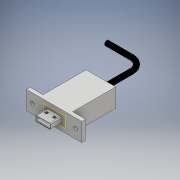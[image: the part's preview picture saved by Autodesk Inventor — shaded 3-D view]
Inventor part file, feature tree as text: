
AUTODESK INVENTOR PART (.ipt)
format: ipt  version: 2018 (Build 220112000, 112)  size: 487,424 bytes
history: native  units: mm
features: sketch x15, extrude x12, fillet x4, plane x2, projected_geometry x2, chamfer x1, sweep x1
ambient origin geometry x8: Origin, YZ Plane, XZ Plane, XY Plane, X Axis, Y Axis, Z Axis, Center Point
bodies: Solid1 (feature_tree)
feature tree (37):
  extrude  "Extrusion1"  Depth=20.88mm
  chamfer  "Chamfer1"  Distance=8.0mm
  fillet  "Fillet1"  Radius=0.5mm
  fillet  "Fillet2"  Radius=3.0mm
  fillet  "Fillet3"  Radius=3.0mm
  extrude  "Extrusion2"  Depth=14.9mm
  extrude  "Extrusion3"  Depth=12.0mm TaperAngle=0.0deg
  fillet  "Fillet4"  Radius=12.0mm
  extrude  "Extrusion4"  Depth=12.0mm TaperAngle=0.0deg
  extrude  "Extrusion5"  Depth=5.0mm
  extrude  "Extrusion6"  Depth=2.0mm
  extrude  "Extrusion7"  Depth=1.8mm
  extrude  "Extrusion8"  Depth=2.45mm TaperAngle=0.0deg
  extrude  "Extrusion9"  Depth=0.2mm TaperAngle=0.0deg
  sketch  "Sketch11"  dims[d27=2.0mm d28=1.8mm]
  plane  "Work Plane1"
  sweep  "Sweep1"
  plane  "Work Plane2"
  sketch  "Sketch13"  dims[d32=0.3mm d33=0.2mm d34=0.0mm]
  extrude  "Extrusion10"  Depth=9.0mm TaperAngle=0.0deg
  extrude  "Extrusion11"  Depth=3.0mm
  extrude  "Extrusion12"  Depth=3.0mm
  sketch  "Sketch1"  dims[d2=16.16mm d3=20.88mm]
  sketch  "Sketch2"  dims[d4=10.8mm]
  sketch  "Sketch4"  dims[d5=10.6mm d6=8.0mm d7=0.0mm]
  sketch  "Sketch5"  dims[d8=1.0mm d9=2.0mm d10=45.0deg d11=0.5mm d12=3.0mm d13=3.0mm]
  sketch  "Sketch6"  dims[d14=7.75mm d15=14.9mm]
  projected_geometry  "Projected Loop1"
  sketch  "Sketch7"  dims[d16=2.3mm d17=0.3mm d18=0.0mm d19=12.0mm]
  sketch  "Sketch8"  dims[d20=4.5mm d21=12.0mm d22=0.0mm]
  sketch  "Sketch9"  dims[d23=0.75mm d24=5.0mm]
  projected_geometry  "Projected Loop2"
  sketch  "Sketch10"  dims[d25=5.0mm d26=2.0mm]
  sketch  "Sketch12"  dims[d29=1.8mm d30=2.45mm d31=0.0mm]
  sketch  "Sketch14"  dims[d35=0.801472mm d36=0.001mm]
  sketch  "Sketch15"  dims[d37=9.0mm d38=0.0mm d71=0.3mm d72=0.0mm]
  sketch  "Sketch16"  dims[d73=7.4mm d74=8.3mm d75=-0.872665mm d76=3.9mm d77=20.0mm d78=0.0mm d79=10.0mm d80=30.0mm d81=10.0mm d82=0.0mm d83=0.0mm d84=3.0mm d85=12.4mm d86=4.9mm d87=45.0mm d88=15.0mm d89=3.0mm d90=0.0mm d91=24.0mm d92=17.0mm d93=9.0mm d94=35.0mm d95=0.0mm d96=3.2mm d97=5.0mm d98=3.0mm d99=0.0mm]
